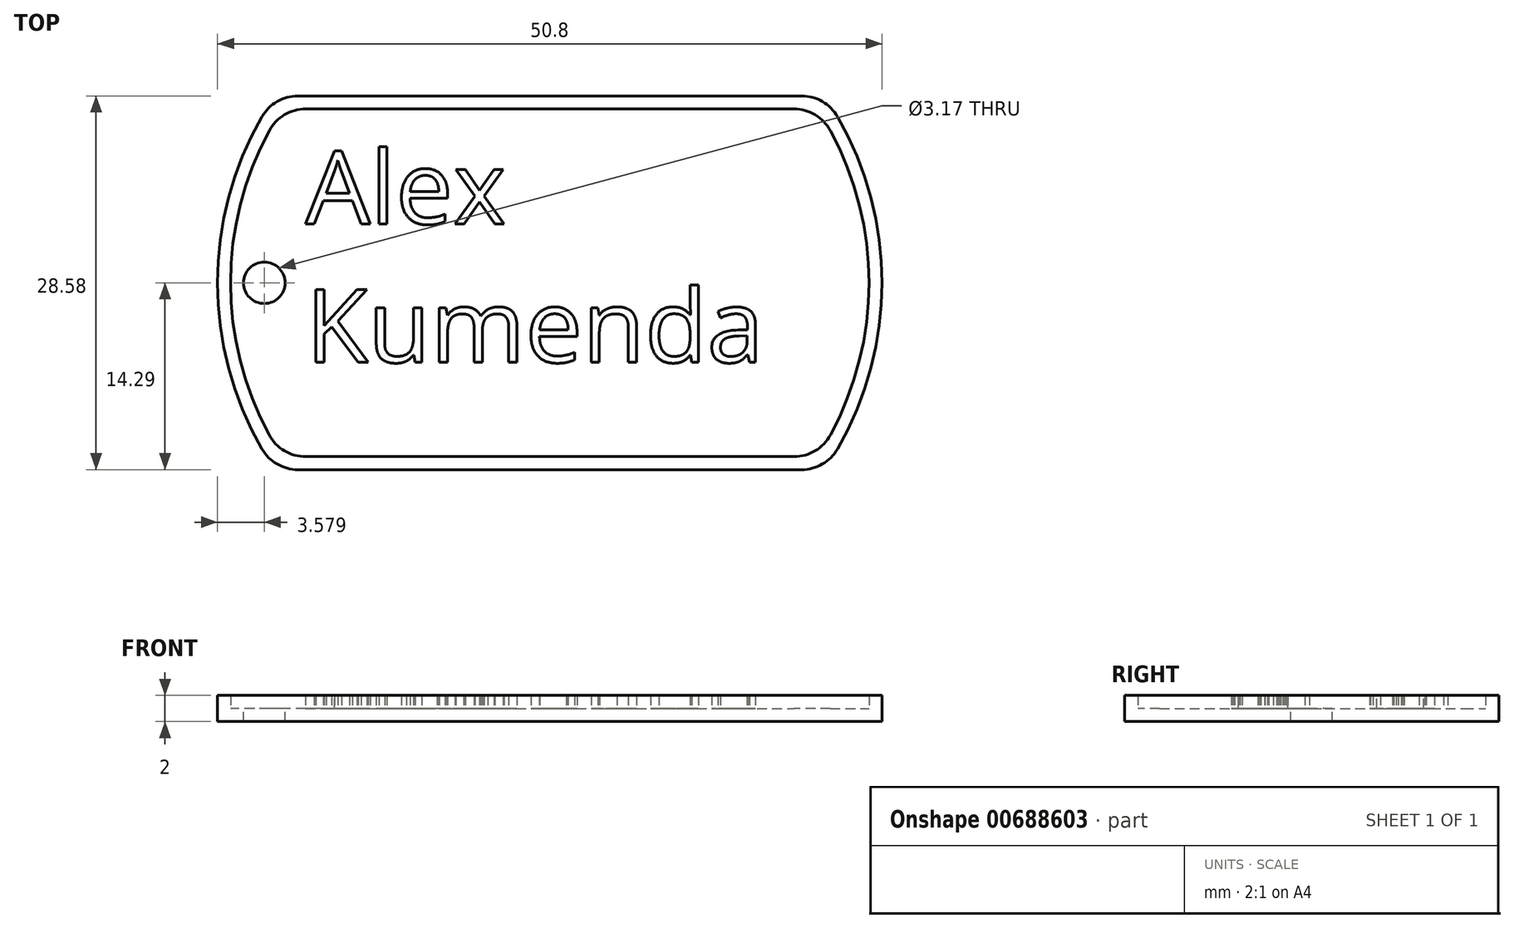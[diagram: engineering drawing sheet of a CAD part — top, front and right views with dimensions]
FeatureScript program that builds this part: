
annotation { "Feature Type Name" : "Feature", "Feature Type Description" : "" }
export const myFeature = defineFeature(function(context is Context, id is Id, definition is map)
    precondition{}
    {
        {
            var Q0;
            Q0=qCreatedBy(makeId("Top.planeOp"),FACE);
            var sketch = newSketch(context, id + "F0", { "sketchPlane" : qUnion([Q0])});
            skArc(sketch, "E0", {"start": v(-22, 12.7) * mm, "mid": v(-25.4, 0) * mm, "end": v(-22, -12.7) * mm});
            skLineSegment(sketch, "E1.top", {"start": v(-19.25, -14.29) * mm, "end": v(19.25, -14.29) * mm});
            skArc(sketch, "E2.trimOffspring", {"start": v(22, -12.7) * mm, "mid": v(25.4, 0) * mm, "end": v(22, 12.7) * mm});
            skLineSegment(sketch, "E3", {"start": v(-19.25, 14.29) * mm, "end": v(19.25, 14.29) * mm});
            skPoint(sketch, "E4.visualSharp", {"position": v(-21, 14.29) * mm});
            skArc(sketch, "E4.filletArc", {"start": v(-19.25, 14.29) * mm, "mid": v(-20.83, 13.86) * mm, "end": v(-22, 12.7) * mm});
            skPoint(sketch, "E5.visualSharp", {"position": v(21, 14.29) * mm});
            skArc(sketch, "E5.filletArc", {"start": v(22, 12.7) * mm, "mid": v(20.83, 13.86) * mm, "end": v(19.25, 14.29) * mm});
            skPoint(sketch, "E6.visualSharp", {"position": v(21, -14.29) * mm});
            skArc(sketch, "E6.filletArc", {"start": v(19.25, -14.29) * mm, "mid": v(20.83, -13.86) * mm, "end": v(22, -12.7) * mm});
            skPoint(sketch, "E7.visualSharp", {"position": v(-21, -14.29) * mm});
            skArc(sketch, "E7.filletArc", {"start": v(-22, -12.7) * mm, "mid": v(-20.83, -13.86) * mm, "end": v(-19.25, -14.29) * mm});
            skSolve(sketch);
        }
        {
            var Q0;
            Q0=makeQuery(id+"F0.imprint","IMPRINT",FACE,{"disambiguationData":[TD([[makeQuery(id+"F0.imprint","IMPRINT",EDGE,{"derivedFrom":sQuery(id+"F0.wireOp",EDGE,"E0")}),1.0]])]});
            extrude(context, id + "F1", {"entities" : qUnion([Q0]), "depth" : 1 * mm, "offsetDistance" : 25.4 * mm});
        }
        {
            var Q0;
            Q0=makeQuery(id+"F1.opExtrude","CAP_FACE",FACE,{"disambiguationData":[OSD([sQuery(id+"F0.wireOp",EDGE,"E0"),sQuery(id+"F0.wireOp",EDGE,"E1.top"),sQuery(id+"F0.wireOp",EDGE,"E2.trimOffspring"),sQuery(id+"F0.wireOp",EDGE,"E3"),sQuery(id+"F0.wireOp",EDGE,"E4.filletArc"),sQuery(id+"F0.wireOp",EDGE,"E5.filletArc"),sQuery(id+"F0.wireOp",EDGE,"E6.filletArc"),sQuery(id+"F0.wireOp",EDGE,"E7.filletArc")])],"isStart":false});
            var sketch = newSketch(context, id + "F2", { "sketchPlane" : qUnion([Q0])});
            skLineSegment(sketch, "E8.0", {"start": v(-18.66, 13.29) * mm, "end": v(18.66, 13.29) * mm});
            skArc(sketch, "E8.1", {"start": v(-21.45, 11.63) * mm, "mid": v(-24.4, 0) * mm, "end": v(-21.45, -11.63) * mm});
            skLineSegment(sketch, "E8.2", {"start": v(-18.66, -13.29) * mm, "end": v(18.66, -13.29) * mm});
            skArc(sketch, "E8.3", {"start": v(21.45, -11.63) * mm, "mid": v(24.4, 0) * mm, "end": v(21.45, 11.63) * mm});
            skPoint(sketch, "E9.visualSharp", {"position": v(-20.46, 13.29) * mm});
            skArc(sketch, "E9.filletArc", {"start": v(-18.66, 13.29) * mm, "mid": v(-20.29, 12.84) * mm, "end": v(-21.45, 11.63) * mm});
            skPoint(sketch, "E10.visualSharp", {"position": v(20.46, 13.29) * mm});
            skArc(sketch, "E10.filletArc", {"start": v(21.45, 11.63) * mm, "mid": v(20.29, 12.84) * mm, "end": v(18.66, 13.29) * mm});
            skPoint(sketch, "E11.visualSharp", {"position": v(20.46, -13.29) * mm});
            skArc(sketch, "E11.filletArc", {"start": v(18.66, -13.29) * mm, "mid": v(20.29, -12.84) * mm, "end": v(21.45, -11.63) * mm});
            skPoint(sketch, "E12.visualSharp", {"position": v(-20.46, -13.29) * mm});
            skArc(sketch, "E12.filletArc", {"start": v(-21.45, -11.63) * mm, "mid": v(-20.29, -12.84) * mm, "end": v(-18.66, -13.29) * mm});
            skLineSegment(sketch, "E13.0", {"start": v(-19.25, 14.29) * mm, "end": v(19.25, 14.29) * mm});
            skArc(sketch, "E13.1", {"start": v(-22, 12.7) * mm, "mid": v(-25.4, 0) * mm, "end": v(-22, -12.7) * mm});
            skLineSegment(sketch, "E13.2", {"start": v(-19.25, -14.29) * mm, "end": v(19.25, -14.29) * mm});
            skArc(sketch, "E13.3", {"start": v(22, -12.7) * mm, "mid": v(25.4, 0) * mm, "end": v(22, 12.7) * mm});
            skPoint(sketch, "E14.visualSharp", {"position": v(-21, -14.29) * mm});
            skArc(sketch, "E14.filletArc", {"start": v(-22, -12.7) * mm, "mid": v(-20.83, -13.86) * mm, "end": v(-19.25, -14.29) * mm});
            skPoint(sketch, "E15.visualSharp", {"position": v(21, -14.29) * mm});
            skArc(sketch, "E15.filletArc", {"start": v(19.25, -14.29) * mm, "mid": v(20.83, -13.86) * mm, "end": v(22, -12.7) * mm});
            skPoint(sketch, "E16.visualSharp", {"position": v(21, 14.29) * mm});
            skArc(sketch, "E16.filletArc", {"start": v(22, 12.7) * mm, "mid": v(20.83, 13.86) * mm, "end": v(19.25, 14.29) * mm});
            skPoint(sketch, "E17.visualSharp", {"position": v(-21, 14.29) * mm});
            skArc(sketch, "E17.filletArc", {"start": v(-19.25, 14.29) * mm, "mid": v(-20.83, 13.86) * mm, "end": v(-22, 12.7) * mm});
            skSolve(sketch);
        }
        {
            var Q0;
            Q0=makeQuery(id+"F2.imprint","IMPRINT",FACE,{"disambiguationData":[TD([[makeQuery(id+"F2.imprint","IMPRINT",EDGE,{"derivedFrom":sQuery(id+"F2.wireOp",EDGE,"E8.0")}),1.0]])]});
            extrude(context, id + "F3", {"entities" : qUnion([Q0]), "operationType" : NewBodyOperationType.ADD, "depth" : 1 * mm, "offsetDistance" : 25.4 * mm});
        }
        {
            var Q0;
            Q0=makeQuery(id+"F1.opExtrude","CAP_FACE",FACE,{"disambiguationData":[OSD([sQuery(id+"F0.wireOp",EDGE,"E0"),sQuery(id+"F0.wireOp",EDGE,"E1.top"),sQuery(id+"F0.wireOp",EDGE,"E2.trimOffspring"),sQuery(id+"F0.wireOp",EDGE,"E3"),sQuery(id+"F0.wireOp",EDGE,"E4.filletArc"),sQuery(id+"F0.wireOp",EDGE,"E5.filletArc"),sQuery(id+"F0.wireOp",EDGE,"E6.filletArc"),sQuery(id+"F0.wireOp",EDGE,"E7.filletArc")])],"isStart":false});
            var sketch = newSketch(context, id + "F4", { "sketchPlane" : qUnion([Q0])});
            skCircle(sketch, "E18", {"center": v(-21.82, 0) * mm, "radius": 1.59 * mm});
            skSolve(sketch);
        }
        {
            var Q0;
            Q0=makeQuery(id+"F4.imprint","IMPRINT",FACE,{"disambiguationData":[TD([[makeQuery(id+"F4.imprint","IMPRINT",EDGE,{"derivedFrom":sQuery(id+"F4.wireOp",EDGE,"E18")}),1.0]])]});
            extrude(context, id + "F5", {"entities" : qUnion([Q0]), "operationType" : NewBodyOperationType.REMOVE, "oppositeDirection" : true, "depth" : 1 * mm, "offsetDistance" : 25.4 * mm});
        }
        {
            var Q0;
            Q0=makeQuery(id+"F1.opExtrude","CAP_FACE",FACE,{"disambiguationData":[OSD([sQuery(id+"F0.wireOp",EDGE,"E0"),sQuery(id+"F0.wireOp",EDGE,"E1.top"),sQuery(id+"F0.wireOp",EDGE,"E2.trimOffspring"),sQuery(id+"F0.wireOp",EDGE,"E3"),sQuery(id+"F0.wireOp",EDGE,"E4.filletArc"),sQuery(id+"F0.wireOp",EDGE,"E5.filletArc"),sQuery(id+"F0.wireOp",EDGE,"E6.filletArc"),sQuery(id+"F0.wireOp",EDGE,"E7.filletArc")])],"isStart":false});
            var sketch = newSketch(context, id + "F6", { "sketchPlane" : qUnion([Q0])});
            skText(sketch, "E19", { "text": "Alex\nKumenda", "fontName": "OpenSans-Regular.ttf"});
            const initialGuessF6  = {"E19": [-0.01866, 0.0045, 1, 0, 0.0056]};
            skSetInitialGuess(sketch, initialGuessF6);
            skSolve(sketch);
        }
        {
            var Q0;
            Q0 = qSketchRegion(id + "F6", true);
            extrude(context, id + "F7", {"entities" : qUnion([Q0]), "operationType" : NewBodyOperationType.ADD, "depth" : 1 * mm, "offsetDistance" : 25.4 * mm});
        }
    });
